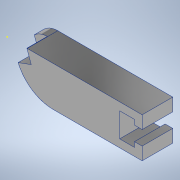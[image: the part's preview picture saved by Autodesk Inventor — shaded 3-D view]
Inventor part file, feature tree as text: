
AUTODESK INVENTOR PART (.ipt)
format: ipt  version: 2022 (Build 260153000, 153)  size: 164,352 bytes
history: native  units: mm
features: sketch x4, extrude x3, fillet x1
ambient origin geometry x8: Origin, YZ Plane, XZ Plane, XY Plane, X Axis, Y Axis, Z Axis, Center Point
bodies: Body1 (feature_tree)
feature tree (8):
  extrude  "Extrusion2"  Depth=5.8mm
  extrude  "Extrusion6"  Depth=12.0mm
  extrude  "Extrusion8"  TaperAngle=0.0deg  [1 undecoded]
  fillet  "Fillet2"  Radius=36.2mm
  sketch  "Sketch12"  dims[d85=5.6mm d86=9.5mm d87=3.0mm d89=5.0mm d90=8.0mm d91=0.0mm d92=19.198622mm d93=10.0mm d98=5.5mm d99=0.0mm d100=0.0mm d101=15.0mm]
  sketch  "Sketch5"  dims[d41=5.8mm d48=44.0mm]
  sketch  "Sketch9"  dims[d56=12.0mm d57=0.0mm d63=45.0mm]
  sketch  "Sketch11"  dims[d67=15.6mm d71=0.0mm d72=36.2mm]
note: 1 required parameter value undecoded (feature->parameter linkage not recoverable at this tier; creation-order binding heuristic only, values carry confidence <= 0.55)
